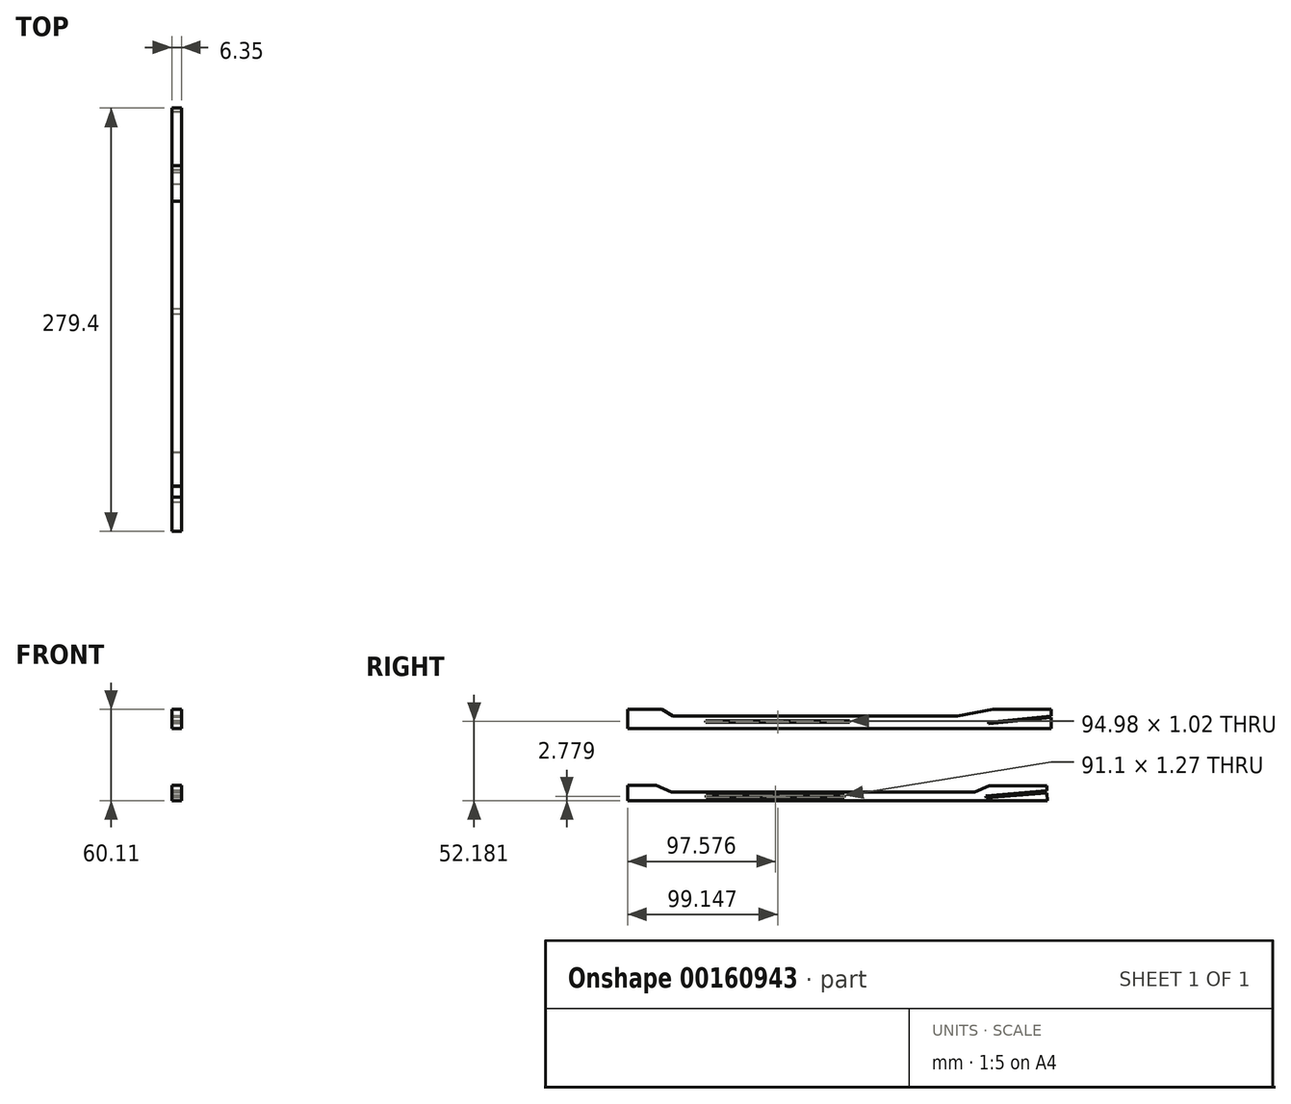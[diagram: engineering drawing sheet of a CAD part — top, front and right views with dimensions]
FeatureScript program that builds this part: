
annotation { "Feature Type Name" : "Feature", "Feature Type Description" : "" }
export const myFeature = defineFeature(function(context is Context, id is Id, definition is map)
    precondition{}
    {
        {
            var Q0;
            Q0=qCreatedBy(makeId("Right.planeOp"),FACE);
            var sketch = newSketch(context, id + "F0", { "sketchPlane" : qUnion([Q0])});
            skLineSegment(sketch, "E0", {"start": v(-76.64, -60.1) * mm, "end": v(-76.64, -49.95) * mm});
            skLineSegment(sketch, "E1", {"start": v(-76.64, -49.95) * mm, "end": v(-57.84, -49.95) * mm});
            skLineSegment(sketch, "E2", {"start": v(-57.84, -49.95) * mm, "end": v(-47.88, -54.58) * mm});
            skLineSegment(sketch, "E3", {"start": v(-47.88, -54.58) * mm, "end": v(152.3, -54.58) * mm});
            skLineSegment(sketch, "E4", {"start": v(152.3, -54.58) * mm, "end": v(161.7, -50.43) * mm});
            skLineSegment(sketch, "E5", {"start": v(161.7, -50.43) * mm, "end": v(199.86, -50.43) * mm});
            skLineSegment(sketch, "E6", {"start": v(-76.64, -60.1) * mm, "end": v(200.13, -60.1) * mm});
            skLineSegment(sketch, "E7", {"start": v(200.13, -60.1) * mm, "end": v(199.86, -50.43) * mm});
            skLineSegment(sketch, "E8", {"start": v(199.95, -53.7) * mm, "end": v(159.68, -57.03) * mm});
            skLineSegment(sketch, "E9", {"start": v(159.68, -57.03) * mm, "end": v(159.8, -58.42) * mm});
            skLineSegment(sketch, "E10", {"start": v(159.8, -58.42) * mm, "end": v(200, -55.1) * mm});
            skLineSegment(sketch, "E11", {"start": v(-24.8, -56.7) * mm, "end": v(-24.8, -57.97) * mm});
            skLineSegment(sketch, "E12", {"start": v(-24.8, -57.97) * mm, "end": v(66.3, -57.97) * mm});
            skLineSegment(sketch, "E13", {"start": v(66.3, -57.97) * mm, "end": v(66.3, -56.7) * mm});
            skLineSegment(sketch, "E14", {"start": v(66.3, -56.7) * mm, "end": v(-24.8, -56.7) * mm});
            skSolve(sketch);
        }
        {
            var Q0;
            Q0=makeQuery(id+"F0.imprint","IMPRINT",FACE,{"disambiguationData":[TD([[makeQuery(id+"F0.imprint","IMPRINT",EDGE,{"derivedFrom":sQuery(id+"F0.wireOp",EDGE,"E0")}),-1.0]])]});
            extrude(context, id + "F1", {"entities" : qUnion([Q0]), "depth" : 6.35 * mm});
        }
        {
            var Q0;
            Q0=qCreatedBy(makeId("Right.planeOp"),FACE);
            var sketch = newSketch(context, id + "F2", { "sketchPlane" : qUnion([Q0])});
            skLineSegment(sketch, "E15", {"start": v(-76.82, 0) * mm, "end": v(-76.82, -12.7) * mm});
            skLineSegment(sketch, "E16", {"start": v(-76.82, -12.7) * mm, "end": v(202.58, -12.7) * mm});
            skLineSegment(sketch, "E17", {"start": v(202.58, -12.7) * mm, "end": v(202.58, 0) * mm});
            skLineSegment(sketch, "E18", {"start": v(202.58, 0) * mm, "end": v(164.48, 0) * mm});
            skLineSegment(sketch, "E19", {"start": v(164.48, 0) * mm, "end": v(140.9, -4.25) * mm});
            skLineSegment(sketch, "E20", {"start": v(140.9, -4.25) * mm, "end": v(-46.78, -4.25) * mm});
            skLineSegment(sketch, "E21", {"start": v(-46.78, -4.25) * mm, "end": v(-54.2, 0) * mm});
            skLineSegment(sketch, "E22", {"start": v(-54.2, 0) * mm, "end": v(-76.82, 0) * mm});
            skLineSegment(sketch, "E23", {"start": v(-25.16, -7.42) * mm, "end": v(-25.16, -8.44) * mm});
            skLineSegment(sketch, "E24", {"start": v(-25.16, -7.42) * mm, "end": v(69.81, -7.42) * mm});
            skLineSegment(sketch, "E25", {"start": v(69.81, -7.42) * mm, "end": v(69.81, -8.44) * mm});
            skLineSegment(sketch, "E26", {"start": v(69.81, -8.44) * mm, "end": v(-25.16, -8.44) * mm});
            skLineSegment(sketch, "E27", {"start": v(202.58, -4.25) * mm, "end": v(161.42, -8.44) * mm});
            skLineSegment(sketch, "E28", {"start": v(161.42, -8.44) * mm, "end": v(161.53, -9.45) * mm});
            skLineSegment(sketch, "E29", {"start": v(161.53, -9.45) * mm, "end": v(202.58, -5.27) * mm});
            skLineSegment(sketch, "E30", {"start": v(202.58, -5.27) * mm, "end": v(202.58, -4.25) * mm});
            skSolve(sketch);
        }
        {
            var Q0;
            Q0=makeQuery(id+"F2.imprint","IMPRINT",FACE,{"disambiguationData":[TD([[makeQuery(id+"F2.imprint","IMPRINT",EDGE,{"derivedFrom":sQuery(id+"F2.wireOp",EDGE,"E15")}),1.0]])]});
            extrude(context, id + "F3", {"entities" : qUnion([Q0]), "depth" : 6.35 * mm});
        }
    });
